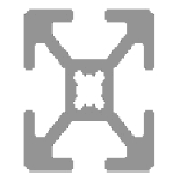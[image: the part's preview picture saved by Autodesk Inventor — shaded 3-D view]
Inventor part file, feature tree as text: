
AUTODESK INVENTOR PART (.ipt)
format: ipt  version: 2013 SP2 (Build 170200200, 200)  size: 234,496 bytes
history: native  units: in
note: dims shown in document units (in); Inventor stores cm internally (conversion verified against a paired STEP export)
features: other x5, sketch x3, plane x1
ambient origin geometry x8: Origin, YZ Plane, XZ Plane, XY Plane, X Axis, Y Axis, Z Axis, Center Point
bodies: Solid1 (feature_tree), Body (feature_tree)
feature tree (9):
  other  "Driven Length"
  other  "Frame Generator"
  other  "Blocks"
  other  "Start Plane"
  other  "End Plane"
  sketch  "Sketch"  dims[d4=0.13in d5=0.0in d6=90.0deg d7=16.5354in]
  sketch  "Sketch2"  dims[d2=0.7874in]
  plane  "Work Plane3"
  sketch  "Sketch3"  dims[d3=17.3228in]
